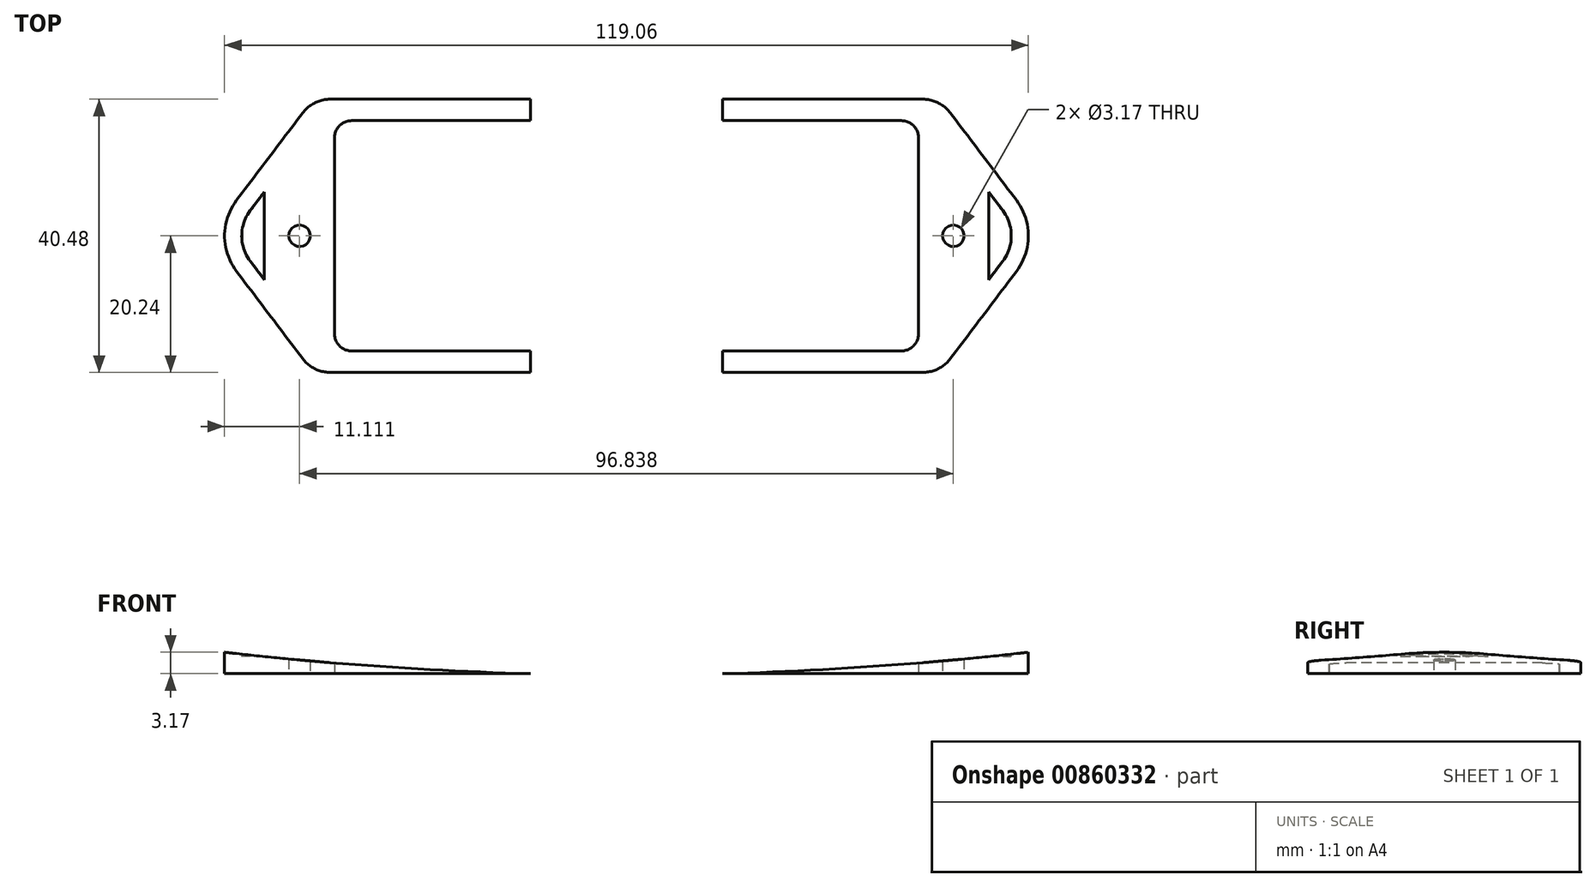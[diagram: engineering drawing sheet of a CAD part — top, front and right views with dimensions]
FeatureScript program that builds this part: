
annotation { "Feature Type Name" : "Feature", "Feature Type Description" : "" }
export const myFeature = defineFeature(function(context is Context, id is Id, definition is map)
    precondition{}
    {
        {
            var Q0;
            Q0=qCreatedBy(makeId("Top.planeOp"),FACE);
            var sketch = newSketch(context, id + "F0", { "sketchPlane" : qUnion([Q0])});
            skLineSegment(sketch, "E0.bottom", {"start": v(43.26, -17.07) * mm, "end": v(-43.26, -17.07) * mm});
            skLineSegment(sketch, "E0.top", {"start": v(43.26, 17.07) * mm, "end": v(-43.26, 17.07) * mm});
            skLineSegment(sketch, "E0.left", {"start": v(43.26, -17.07) * mm, "end": v(43.26, 17.07) * mm});
            skLineSegment(sketch, "E0.right", {"start": v(-43.26, -17.07) * mm, "end": v(-43.26, 17.07) * mm});
            skPoint(sketch, "E0.middle", {"position": v(0, 0) * mm});
            skLineSegment(sketch, "E1.bottom", {"start": v(46.43, -20.24) * mm, "end": v(-46.43, -20.24) * mm});
            skLineSegment(sketch, "E1.top", {"start": v(46.43, 20.24) * mm, "end": v(-46.43, 20.24) * mm});
            skLineSegment(sketch, "E2", {"start": v(59.53, 27.31) * mm, "end": v(59.53, -36.65) * mm});
            skLineSegment(sketch, "E3.MirrorCS", {"start": v(-59.53, 27.31) * mm, "end": v(-59.53, -36.65) * mm});
            skArc(sketch, "E4", {"start": v(57.76, -5.27) * mm, "mid": v(59.53, 0) * mm, "end": v(57.76, 5.27) * mm});
            skLineSegment(sketch, "E5", {"start": v(46.43, 20.24) * mm, "end": v(57.76, 5.27) * mm});
            skLineSegment(sketch, "E6", {"start": v(46.43, -20.24) * mm, "end": v(57.76, -5.27) * mm});
            skCircle(sketch, "E7", {"center": v(48.42, 0) * mm, "radius": 1.59 * mm});
            skLineSegment(sketch, "E8.MirrorCS", {"start": v(-46.43, 20.24) * mm, "end": v(-57.76, 5.27) * mm});
            skArc(sketch, "E9.MirrorCS", {"start": v(-57.76, -5.27) * mm, "mid": v(-59.53, 0) * mm, "end": v(-57.76, 5.27) * mm});
            skLineSegment(sketch, "E10.MirrorCS", {"start": v(-46.43, -20.24) * mm, "end": v(-57.76, -5.27) * mm});
            skCircle(sketch, "E11.MirrorC", {"center": v(-48.42, 0) * mm, "radius": 1.59 * mm});
            skSolve(sketch);
        }
        {
            var Q0;
            Q0 = qSketchRegion(id + "F0", true);
            extrude(context, id + "F1", {"entities" : qUnion([Q0]), "depth" : 11.9 * mm, "offsetDistance" : 25.4 * mm});
        }
        {
            var Q0;
            Q0=makeQuery(id+"F1.opExtrude","SWEPT_EDGE",EDGE,{"disambiguationData":[OSD([sQuery(id+"F0.wireOp",EDGE,"E1.bottom"),sQuery(id+"F0.wireOp",EDGE,"E10.MirrorCS")])]});
            var Q1;
            Q1=makeQuery(id+"F1.opExtrude","SWEPT_EDGE",EDGE,{"disambiguationData":[OSD([sQuery(id+"F0.wireOp",EDGE,"E1.bottom"),sQuery(id+"F0.wireOp",EDGE,"E6")])]});
            var Q2;
            Q2=makeQuery(id+"F1.opExtrude","SWEPT_EDGE",EDGE,{"disambiguationData":[OSD([sQuery(id+"F0.wireOp",EDGE,"E1.top"),sQuery(id+"F0.wireOp",EDGE,"E5")])]});
            var Q3;
            Q3=makeQuery(id+"F1.opExtrude","SWEPT_EDGE",EDGE,{"disambiguationData":[OSD([sQuery(id+"F0.wireOp",EDGE,"E1.top"),sQuery(id+"F0.wireOp",EDGE,"E8.MirrorCS")])]});
            fillet(context, id + "F2", {"entities" : qUnion([Q0, Q1, Q2, Q3]), "radius" : 5.08 * mm, "tangentPropagation" : true, "allowEdgeOverflow" : false});
        }
        {
            var Q0;
            Q0=makeQuery(id+"F1.opExtrude","SWEPT_EDGE",EDGE,{"disambiguationData":[OSD([sQuery(id+"F0.wireOp",EDGE,"E0.bottom"),sQuery(id+"F0.wireOp",EDGE,"E0.left")])]});
            var Q1;
            Q1=makeQuery(id+"F1.opExtrude","SWEPT_EDGE",EDGE,{"disambiguationData":[OSD([sQuery(id+"F0.wireOp",EDGE,"E0.top"),sQuery(id+"F0.wireOp",EDGE,"E0.left")])]});
            var Q2;
            Q2=makeQuery(id+"F1.opExtrude","SWEPT_EDGE",EDGE,{"disambiguationData":[OSD([sQuery(id+"F0.wireOp",EDGE,"E0.top"),sQuery(id+"F0.wireOp",EDGE,"E0.right")])]});
            var Q3;
            Q3=makeQuery(id+"F1.opExtrude","SWEPT_EDGE",EDGE,{"disambiguationData":[OSD([sQuery(id+"F0.wireOp",EDGE,"E0.bottom"),sQuery(id+"F0.wireOp",EDGE,"E0.right")])]});
            fillet(context, id + "F3", {"entities" : qUnion([Q0, Q1, Q2, Q3]), "radius" : 2.54 * mm, "tangentPropagation" : true, "allowEdgeOverflow" : false});
        }
        {
            var Q0;
            Q0=makeQuery(id+"F1.opExtrude","SWEPT_FACE",FACE,{"disambiguationData":[OSD([sQuery(id+"F0.wireOp",EDGE,"E1.bottom")])]});
            var sketch = newSketch(context, id + "F4", { "sketchPlane" : qUnion([Q0])});
            skLineSegment(sketch, "E12", {"start": v(-59.53, 0) * mm, "end": v(-59.53, 3.18) * mm, "construction": true});
            skLineSegment(sketch, "E13", {"start": v(59.53, 3.18) * mm, "end": v(59.53, 0) * mm, "construction": true});
            skLineSegment(sketch, "E14", {"start": v(-5.82, -0.2) * mm, "end": v(10.2, -0.2) * mm, "construction": true});
            skArc(sketch, "E15", {"start": v(-59.53, 3.18) * mm, "mid": v(0, -0.2) * mm, "end": v(59.53, 3.17) * mm});
            skPoint(sketch, "E15.third.point", {"position": v(0, -0.2) * mm});
            skLineSegment(sketch, "E16", {"start": v(-59.53, 3.18) * mm, "end": v(-59.53, 15.99) * mm});
            skLineSegment(sketch, "E17", {"start": v(-59.53, 15.99) * mm, "end": v(59.53, 15.99) * mm});
            skLineSegment(sketch, "E18", {"start": v(59.53, 15.99) * mm, "end": v(59.53, 3.18) * mm});
            skSolve(sketch);
        }
        {
            var Q0;
            Q0 = qSketchRegion(id + "F4", true);
            extrude(context, id + "F5", {"entities" : qUnion([Q0]), "operationType" : NewBodyOperationType.REMOVE, "endBound" : BoundingType.THROUGH_ALL, "oppositeDirection" : true, "depth" : 25.4 * mm, "offsetDistance" : 25.4 * mm});
        }
        {
            var Q0;
            Q0=makeQuery(id+"F5.boolean.opBoolean","COPY",FACE,{"derivedFrom":makeQuery(id+"F5.opExtrude","SWEPT_FACE",FACE,{"disambiguationData":[OSD([sQuery(id+"F4.wireOp",EDGE,"E15")])]})});
            shell(context, id + "F6", {"entities" : qUnion([Q0]), "thickness" : 2.54 * mm});
        }
    });
